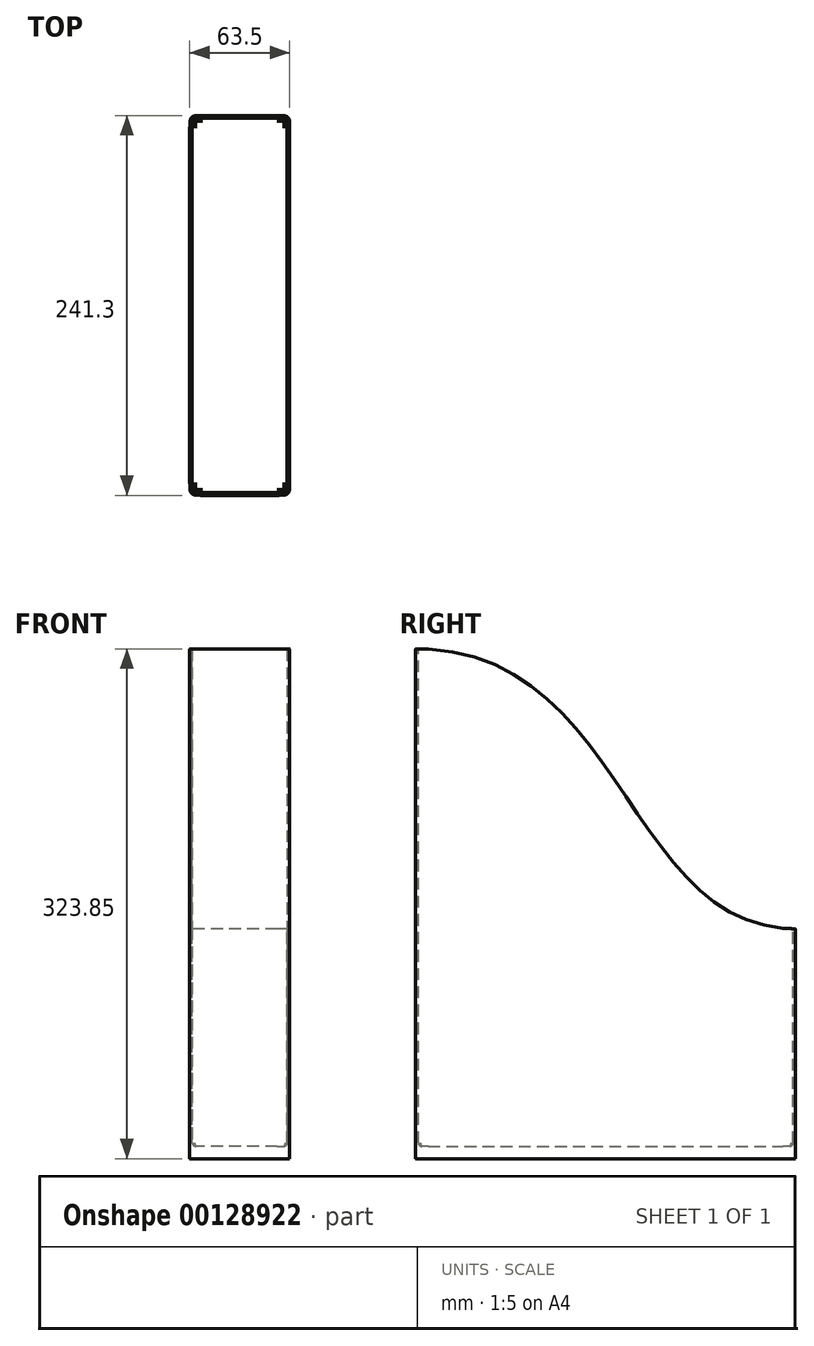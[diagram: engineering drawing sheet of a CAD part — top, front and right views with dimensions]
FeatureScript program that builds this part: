
annotation { "Feature Type Name" : "Feature", "Feature Type Description" : "" }
export const myFeature = defineFeature(function(context is Context, id is Id, definition is map)
    precondition{}
    {
        {
            var Q0;
            Q0=qCreatedBy(makeId("Right.planeOp"),FACE);
            var sketch = newSketch(context, id + "F0", { "sketchPlane" : qUnion([Q0])});
            skLineSegment(sketch, "E0", {"start": v(0, 0) * mm, "end": v(241.3, 0) * mm});
            skLineSegment(sketch, "E1", {"start": v(241.3, 0) * mm, "end": v(241.3, 139.7) * mm});
            skLineSegment(sketch, "E2", {"start": v(0, 317.5) * mm, "end": v(0, 0) * mm});
            skFitSpline(sketch, "E3", {"points": [v(0, 317.5) * mm, v(241.3, 139.7) * mm], "startDerivative": vector(400.05, 0) * mm, "endDerivative": vector(323.85, 0) * mm});
            skLineSegment(sketch, "E4", {"start": v(133.35, 317.5) * mm, "end": v(133.35, 139.7) * mm, "construction": true});
            skSolve(sketch);
        }
        {
            var Q0;
            Q0=qSketchRegion(id+"F0",true);
            extrude(context, id + "F1", {"entities" : qUnion([Q0]), "endBound" : BoundingType.SYMMETRIC, "offsetDistance" : 25.4 * mm, "depth" : 63.5 * mm});
        }
        {
            var Q0;
            Q0=makeQuery(id+"F1.opExtrude","CAP_EDGE",EDGE,{"disambiguationData":[OSD([sQuery(id+"F0.wireOp",EDGE,"E2")])],"isStart":false});
            var Q1;
            Q1=makeQuery(id+"F1.opExtrude","CAP_EDGE",EDGE,{"disambiguationData":[OSD([sQuery(id+"F0.wireOp",EDGE,"E1")])],"isStart":false});
            var Q2;
            Q2=makeQuery(id+"F1.opExtrude","CAP_EDGE",EDGE,{"disambiguationData":[OSD([sQuery(id+"F0.wireOp",EDGE,"E1")])],"isStart":true});
            var Q3;
            Q3=makeQuery(id+"F1.opExtrude","CAP_EDGE",EDGE,{"disambiguationData":[OSD([sQuery(id+"F0.wireOp",EDGE,"E2")])],"isStart":true});
            fillet(context, id + "F2", {"entities" : qUnion([Q0, Q1, Q2, Q3]), "radius" : 8 * mm, "tangentPropagation" : true, "rho" : .7, "crossSection" : FilletCrossSection.CONIC, "allowEdgeOverflow" : false});
        }
        {
            var Q0;
            Q0=makeQuery(id+"F1.opExtrude","SWEPT_FACE",FACE,{"disambiguationData":[OSD([sQuery(id+"F0.wireOp",EDGE,"E3")])]});
            shell(context, id + "F3", {"entities" : qUnion([Q0]), "thickness" : 1.6 * mm});
        }
        {
            var Q0;
            Q0=makeQuery(id+"F3.opShell","OFFSET_FACE",FACE,{"disambiguationData":[OSD([sQuery(id+"F0.wireOp",EDGE,"E0")])]});
            fillet(context, id + "F4", {"entities" : qUnion([Q0]), "radius" : 2 * mm, "tangentPropagation" : true, "allowEdgeOverflow" : false});
        }
        {
            var Q0;
            Q0=makeQuery(id+"F1.opExtrude","SWEPT_FACE",FACE,{"disambiguationData":[OSD([sQuery(id+"F0.wireOp",EDGE,"E0")])]});
            extrude(context, id + "F5", {"entities" : qUnion([Q0]), "operationType" : NewBodyOperationType.ADD, "depth" : 6.35 * mm, "offsetDistance" : 25.4 * mm});
        }
    });
